# Revit family: Franke_A400_NM_Tank(USA)
name_source: partatom
category: Specialty Equipment
revit_build: Autodesk Revit 2015 (Build: 20140606_1530(x64)
units: mm (PartAtom-declared; Revit-internal decimal feet)

## types (2) — shared parameters
Assembly Code = fully automatic coffee machine
Cycle (A400) = 60 Hz
Cycle alternativ (A400) = 0 Hz
Depth (mm) = 600 mm
Description = A400 fully automatic coffee machine
Energy loss acc. to DIN 18873 (A400) = /
Height (mm) = 744 mm  [stored 2.44094 ft]
Keynote = fully automatic coffee machine
Manufacturer = Franke
Max Overcurrent Protection (A400) = 30 A
Model = A400 NM Tank
Noise emission = 70 dB
Number of Nutral Conductors (A400) = /
Number of Poles (A400) = 2
Number of Protective Conductors (A400) = 1
URL = https://www.franke.com
Volts max. (A400) = 220 V
Volts min. (A400) = 200 V
Water pressure = 800000.0 Pa
Water pressure (with filter) = 600000.0 Pa
Watter tank = 4,0 l
Watts max. (A400) = 5300 W
Watts min. (A400) = 4500 W
Weight = 38 kg
Width (mm) = 340 mm  [stored 1.11549 ft]
zero-valued in all types: Cost

## per-type parameters (varying)
| type | Frontcover |
| A400 NM Tank(200-220V/anthracite/USA) | Franke Anthracite |
| A400 NM Tank(200-220V/black line/USA) | Franke Black |

note: [stored X ft] marks values corroborated as IEEE doubles in the binary element streams (Revit-internal decimal feet)

## geometry (parser evidence)
native form markers: Extrusion x1
no freeform markers — native parametric forms only
